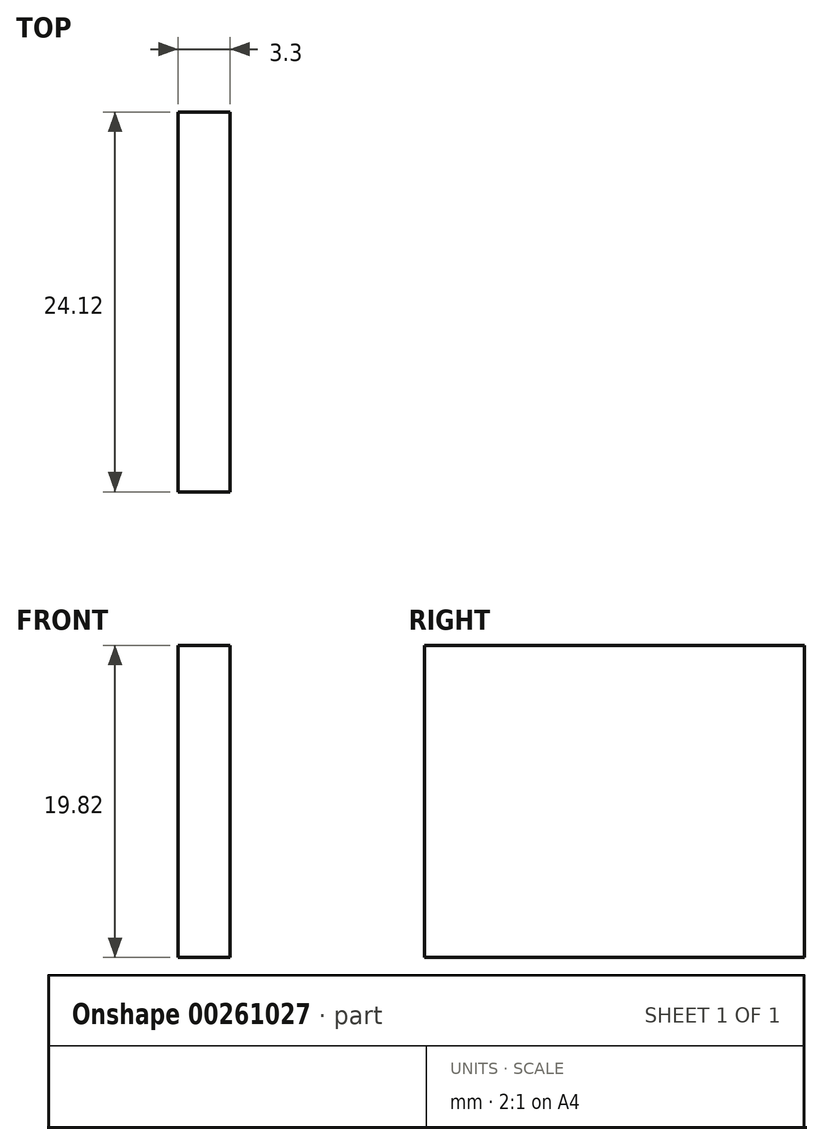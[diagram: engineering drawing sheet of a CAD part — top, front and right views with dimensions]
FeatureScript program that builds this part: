
annotation { "Feature Type Name" : "Feature", "Feature Type Description" : "" }
export const myFeature = defineFeature(function(context is Context, id is Id, definition is map)
    precondition{}
    {
        {
            var Q0;
            Q0=qCreatedBy(makeId("Right.planeOp"),FACE);
            var sketch = newSketch(context, id + "F0", { "sketchPlane" : qUnion([Q0])});
            skLineSegment(sketch, "E0.bottom", {"start": v(12.07, 9.9) * mm, "end": v(-12.07, 9.9) * mm});
            skLineSegment(sketch, "E0.top", {"start": v(12.07, -9.9) * mm, "end": v(-12.07, -9.9) * mm});
            skLineSegment(sketch, "E0.left", {"start": v(12.07, 9.9) * mm, "end": v(12.07, -9.9) * mm});
            skLineSegment(sketch, "E0.right", {"start": v(-12.07, 9.9) * mm, "end": v(-12.07, -9.9) * mm});
            skPoint(sketch, "E0.middle", {"position": v(0, 0) * mm});
            skSolve(sketch);
        }
        {
            var Q0;
            Q0 = qSketchRegion(id + "F0", true);
            extrude(context, id + "F1", {"entities" : qUnion([Q0]), "depth" : 3.3 * mm});
        }
    });
